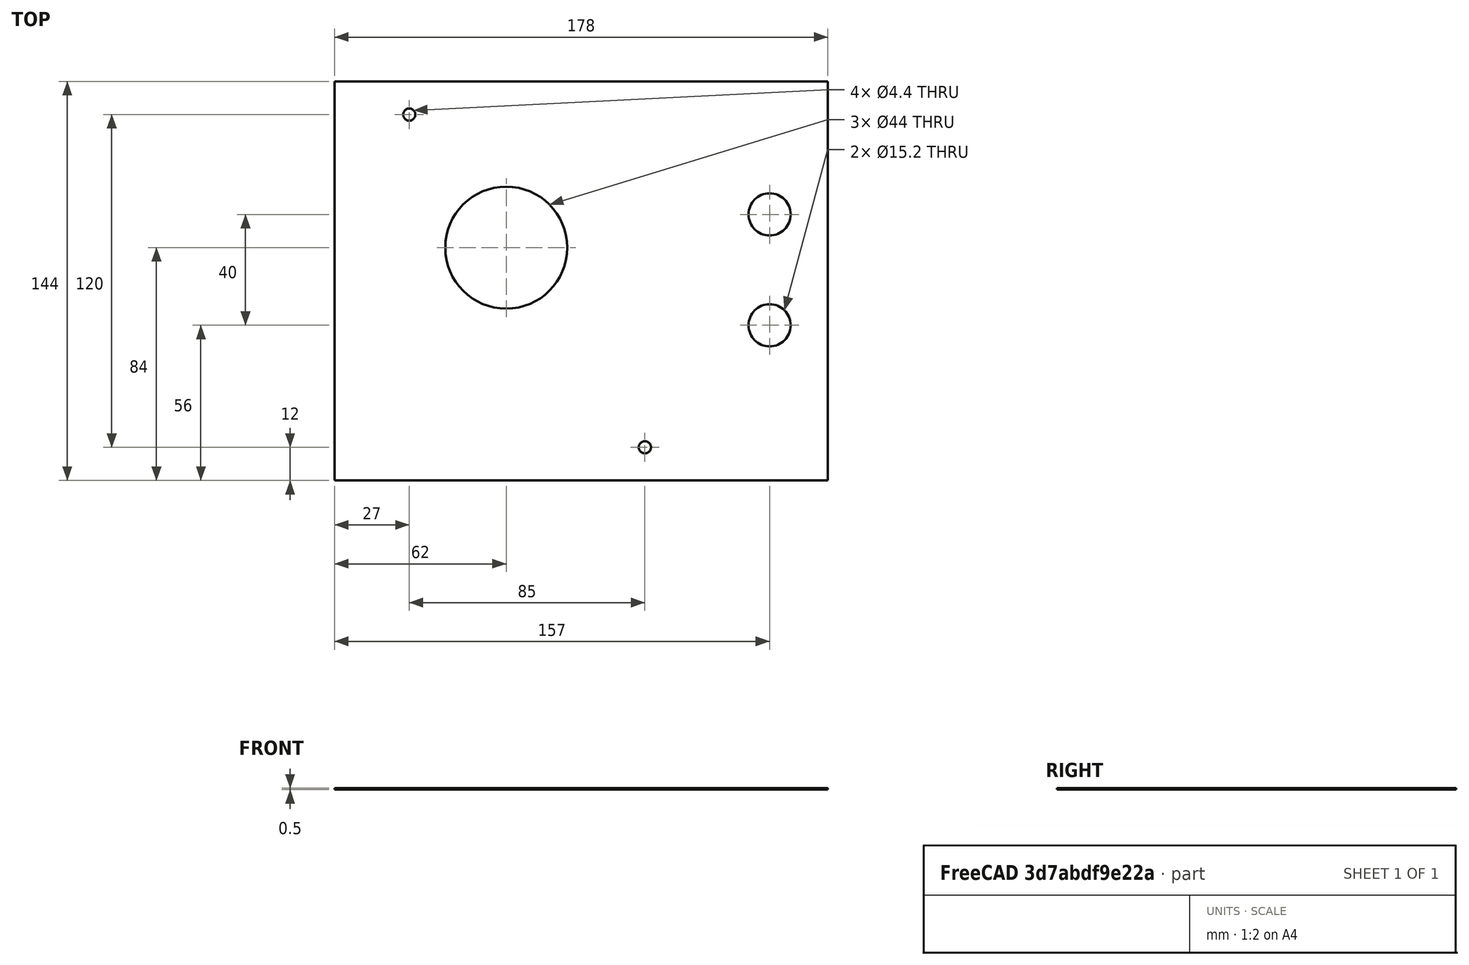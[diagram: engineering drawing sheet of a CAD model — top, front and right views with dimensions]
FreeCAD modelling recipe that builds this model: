
FCSTD DOCUMENT  (FreeCAD 0.17R13026 (Git))
Label: C1080_cover_bottom
License: CreativeCommons Attribution-ShareAlike
LicenseURL: http://creativecommons.org/licenses/by-sa/4.0/
objects: TechDraw::DrawViewDimension×14, Sketcher::SketchObject×3, PartDesign::Pocket×2, PartDesign::Pad×1, TechDraw::DrawSVGTemplate×1, TechDraw::DrawProjGroupItem×1, TechDraw::DrawProjGroup×1, TechDraw::DrawPage×1
note: 9 computed .brp shape members not serialized (recipe doc carries the construction recipe); baked Part::Feature solids carry a one-line shape summary decoded from their .brp

FEATURE [Sketcher::SketchObject] Sketch
  MapMode = 5
  sketch-geometry (5):
    g0: LineSegment StartX=-62 StartY=60 StartZ=0 EndX=116 EndY=60 EndZ=0
    g1: LineSegment StartX=116 StartY=-84 StartZ=0 EndX=-62 EndY=-84 EndZ=0
    g2: LineSegment StartX=-62 StartY=-84 StartZ=0 EndX=-62 EndY=60 EndZ=0
    g3: Circle CenterX=0 CenterY=0 CenterZ=0 NormalX=0 NormalY=0 NormalZ=1 AngleXU=0 Radius=22
    g4: LineSegment StartX=116 StartY=60 StartZ=0 EndX=116 EndY=-84 EndZ=0
  constraints (14):
    c: Coincident(g1,g2)
    c: Coincident(g2,g0)
    c: Horizontal(g0)
    c: Horizontal(g1)
    c: Vertical(g2)
    c: DistanceX(g0,g0) = 178
    c: DistanceY(g1,g0) = 144
    c: Coincident(g3,g-1)
    c: Radius(g3) = 22
    c: DistanceX(g0,g-1) = 62
    c: DistanceY(g-1,g0) = 60
    c: Coincident(g4,g0)
    c: Coincident(g4,g1)
    c: Vertical(g4)
FEATURE [PartDesign::Pad] Pad
  Length = 0.5
  Length2 = 100
  Profile = -> Sketch
  Type = 0
FEATURE [Sketcher::SketchObject] Sketch001  label="Sketch-M4-holes"
  MapMode = 5
  Placement = pos=(0,0,0.5) rot=(0,0,1;0rad)
  Support = -> [Pad]
  sketch-geometry (2):
    g0: Circle CenterX=-35 CenterY=48 CenterZ=0 NormalX=0 NormalY=0 NormalZ=1 AngleXU=0 Radius=2.2
    g1: Circle CenterX=50 CenterY=-72 CenterZ=0 NormalX=0 NormalY=0 NormalZ=1 AngleXU=0 Radius=2.2
  constraints (6):
    c: Equal(g1,g0)
    c: Radius(g0) = 2.2
    c: DistanceX(g0,g-1) = 35
    c: DistanceY(g-1,g0) = 48
    c: DistanceY(g1,g-1) = 72
    c: DistanceX(g-1,g1) = 50
FEATURE [PartDesign::Pocket] Pocket  label="Pocket-M4-holes"
  Length = 5
  Profile = -> Sketch001
  Type = 1
FEATURE [Sketcher::SketchObject] Sketch002
  MapMode = 5
  Placement = pos=(0,0,0.5) rot=(0,0,1;0rad)
  Support = -> [Pocket]
  sketch-geometry (3):
    g0: Circle CenterX=95 CenterY=12 CenterZ=0 NormalX=0 NormalY=0 NormalZ=1 AngleXU=0 Radius=7.6
    g1: Circle CenterX=95 CenterY=-28 CenterZ=0 NormalX=0 NormalY=0 NormalZ=1 AngleXU=0 Radius=7.6
    g2: LineSegment [constr] StartX=95 StartY=12 StartZ=0 EndX=95 EndY=-28 EndZ=0
  constraints (8):
    c: Equal(g0,g1)
    c: Radius(g0) = 7.6
    c: Coincident(g2,g0)
    c: Coincident(g2,g1)
    c: Vertical(g2)
    c: DistanceX(g-1,g0) = 95
    c: DistanceY(g2,g2) = 40
    c: DistanceY(g-1,g0) = 12
FEATURE [PartDesign::Pocket] Pocket001  label="Pocket-cable-gland"
  Length = 5
  Profile = -> Sketch002
  Type = 1
FEATURE [TechDraw::DrawSVGTemplate] Template
  EditableTexts = Designed_by_Name=LSF; Drawing_number=C1080_cover_bottom; FC-Date=27/1/2018; FC-SC=1:2; FC-SH=1/1; FC-Title=C1080_cover_bottom; Subtitle=REV. 2; Weight=-
  Height = 210
  Orientation = 1
  Width = 297
FEATURE [TechDraw::DrawProjGroupItem] ProjItem  label="Front"
  ArcCenterMarks = true
  CenterScale = 2
  Direction = (0,0,-1)
  ExtraWidth = 1.25
  Focus = 100
  HardHidden = false
  HiddenWidth = 0.25
  HorizCenterLine = false
  IsoCount = 0
  IsoHidden = false
  IsoVisible = false
  IsoWidth = 0.25
  KeepLabel = false
  LineWidth = 0.25
  LockPosition = false
  Perspective = false
  Rotation = 0
  RotationVector = (1,0,0)
  ScaleType = 0
  SeamHidden = false
  SeamVisible = false
  ShowSectionLine = true
  SmoothHidden = false
  SmoothVisible = false
  Source = -> [Pocket001]
  Type = 0
  VertCenterLine = false
  X = 0
  Y = 0
FEATURE [TechDraw::DrawProjGroup] ProjGroup
  Anchor = -> ProjItem
  AutoDistribute = true
  CubeDirs = (6) [(0,1,-6.12323e-17),(0,-6.12323e-17,-1),(-1,0,0),(0,6.12323e-17,1),(1,0,0),(0,-1,6.12323e-17)]
  CubeRotations = (6) [(1,0,0),(1,0,0),(0,6.12323e-17,-1),(-1,0,0),(0,-6.12323e-17,1),(1,0,0)]
  KeepLabel = false
  LockPosition = false
  ProjectionType = 0
  Rotation = 0
  Scale = 0.5
  ScaleType = 2
  Source = -> [Pocket001]
  Views = -> [ProjItem]
  X = 156.503
  Y = 142.857
  spacingX = 15
  spacingY = 15
FEATURE [TechDraw::DrawViewDimension] Dimension
  Font = osifont
  Fontsize = 3.5
  FormatSpec = %.2f
  KeepLabel = false
  LineWidth = 0.5
  LockPosition = false
  MeasureType = 1
  References2D = -> [ProjItem]
  Rotation = 0
  ScaleType = 0
  Type = 5
  X = 2.31552
  Y = -15.6743
FEATURE [TechDraw::DrawViewDimension] Dimension001
  Font = osifont
  Fontsize = 3.5
  FormatSpec = %.2f
  KeepLabel = false
  LineWidth = 0.5
  LockPosition = false
  MeasureType = 1
  References2D = -> [ProjItem]
  Rotation = 0
  ScaleType = 0
  Type = 5
  X = -34.3766
  Y = 19.2366
FEATURE [TechDraw::DrawViewDimension] Dimension002
  Font = osifont
  Fontsize = 3.5
  FormatSpec = %.2f
  KeepLabel = false
  LineWidth = 0.5
  LockPosition = false
  MeasureType = 1
  References2D = -> [ProjItem]
  Rotation = 0
  ScaleType = 0
  Type = 5
  X = 9.28566
  Y = -0.299016
FEATURE [TechDraw::DrawViewDimension] Dimension003
  Font = osifont
  Fontsize = 3.5
  FormatSpec = %.2f
  KeepLabel = false
  LineWidth = 0.5
  LockPosition = false
  MeasureType = 1
  References2D = -> [ProjItem]
  Rotation = 0
  ScaleType = 0
  Type = 1
  X = -62.6972
  Y = 52.1883
FEATURE [TechDraw::DrawViewDimension] Dimension004
  Font = osifont
  Fontsize = 3.5
  FormatSpec = %.2f
  KeepLabel = false
  LineWidth = 0.5
  LockPosition = false
  MeasureType = 1
  References2D = -> [ProjItem]
  Rotation = 0
  ScaleType = 0
  Type = 2
  X = -105.267
  Y = 58.0662
FEATURE [TechDraw::DrawViewDimension] Dimension005
  Font = osifont
  Fontsize = 3.5
  FormatSpec = %.2f
  KeepLabel = false
  LineWidth = 0.5
  LockPosition = false
  MeasureType = 1
  References2D = -> [ProjItem]
  Rotation = 0
  ScaleType = 0
  Type = 2
  X = -115.776
  Y = 57.1756
FEATURE [TechDraw::DrawViewDimension] Dimension006
  Font = osifont
  Fontsize = 3.5
  FormatSpec = %.2f
  KeepLabel = false
  LineWidth = 0.5
  LockPosition = false
  MeasureType = 1
  References2D = -> [ProjItem]
  Rotation = 0
  ScaleType = 0
  Type = 1
  X = -61.6285
  Y = 69.8219
FEATURE [TechDraw::DrawViewDimension] Dimension007
  Font = osifont
  Fontsize = 3.5
  FormatSpec = %.2f
  KeepLabel = false
  LineWidth = 0.5
  LockPosition = false
  MeasureType = 1
  References2D = -> [ProjItem]
  Rotation = 0
  ScaleType = 0
  Type = 2
  X = -96.7744
  Y = 55.7368
FEATURE [TechDraw::DrawViewDimension] Dimension008
  Font = osifont
  Fontsize = 3.5
  FormatSpec = %.2f
  KeepLabel = false
  LineWidth = 0.5
  LockPosition = false
  MeasureType = 1
  References2D = -> [ProjItem]
  Rotation = 0
  ScaleType = 0
  Type = 1
  X = -63.0525
  Y = 45.755
FEATURE [TechDraw::DrawViewDimension] Dimension009
  Font = osifont
  Fontsize = 3.5
  FormatSpec = %.2f
  KeepLabel = false
  LineWidth = 0.5
  LockPosition = false
  MeasureType = 1
  References2D = -> [ProjItem]
  Rotation = 0
  ScaleType = 0
  Type = 1
  X = -62.5463
  Y = 60.5944
FEATURE [TechDraw::DrawViewDimension] Dimension010
  Font = osifont
  Fontsize = 3.5
  FormatSpec = %.2f
  KeepLabel = false
  LineWidth = 0.5
  LockPosition = false
  MeasureType = 1
  References2D = -> [ProjItem]
  Rotation = 0
  ScaleType = 0
  Type = 2
  X = 55.3507
  Y = 51.553
FEATURE [TechDraw::DrawViewDimension] Dimension011
  Font = osifont
  Fontsize = 3.5
  FormatSpec = %.2f
  KeepLabel = false
  LineWidth = 0.5
  LockPosition = false
  MeasureType = 1
  References2D = -> [ProjItem]
  Rotation = 0
  ScaleType = 0
  Type = 2
  X = 64.0891
  Y = 52.6082
FEATURE [TechDraw::DrawViewDimension] Dimension012
  Font = osifont
  Fontsize = 3.5
  FormatSpec = %.2f
  KeepLabel = false
  LineWidth = 0.5
  LockPosition = false
  MeasureType = 1
  References2D = -> [ProjItem]
  Rotation = 0
  ScaleType = 0
  Type = 2
  X = 72.3543
  Y = 52.063
FEATURE [TechDraw::DrawViewDimension] Dimension013
  Font = osifont
  Fontsize = 3.5
  FormatSpec = %.2f
  KeepLabel = false
  LineWidth = 0.5
  LockPosition = false
  MeasureType = 1
  References2D = -> [ProjItem]
  Rotation = 0
  ScaleType = 0
  Type = 1
  X = -81.7302
  Y = -46.0317
FEATURE [TechDraw::DrawPage] Page
  KeepUpdated = true
  ProjectionType = 0
  Template = -> Template
  Views = -> [ProjGroup,Dimension,Dimension001,Dimension002,Dimension003,Dimension004,Dimension005,Dimension006,Dimension007,Dimension008,Dimension009,Dimension010,Dimension011,Dimension012,Dimension013]
